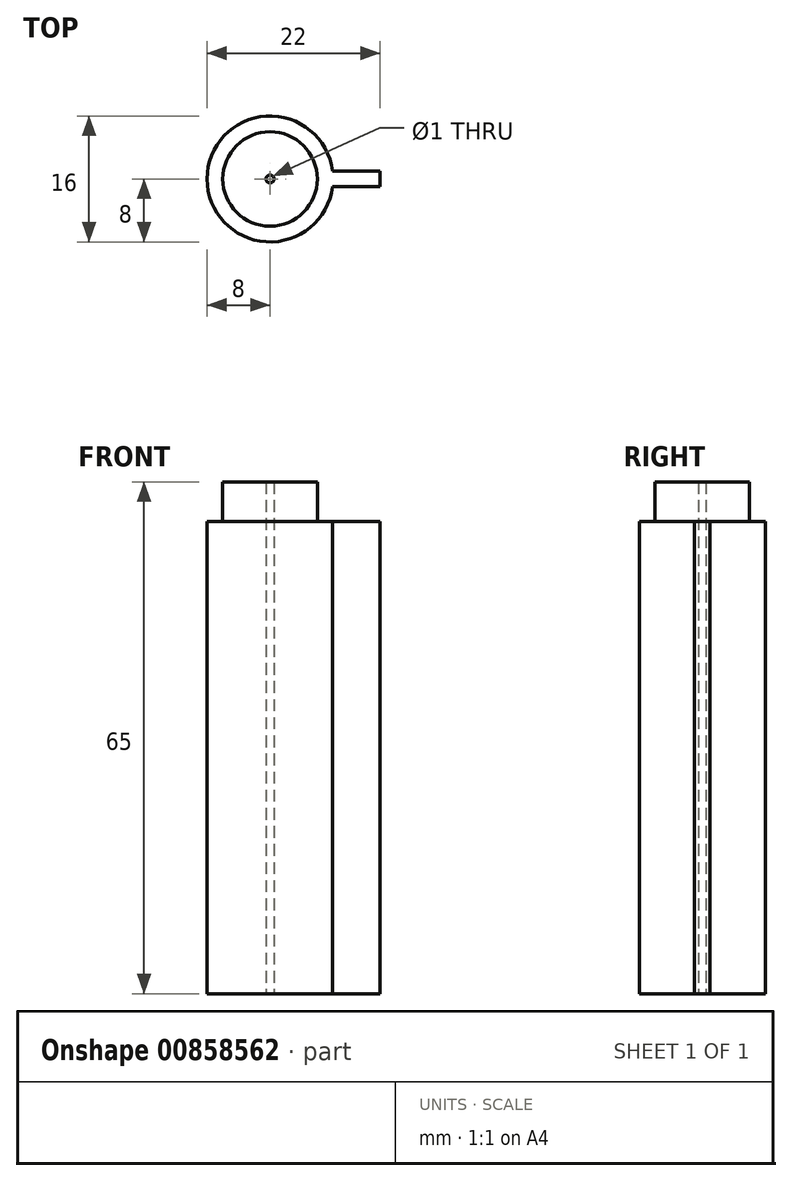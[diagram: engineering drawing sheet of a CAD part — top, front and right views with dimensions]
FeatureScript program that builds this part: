
annotation { "Feature Type Name" : "Feature", "Feature Type Description" : "" }
export const myFeature = defineFeature(function(context is Context, id is Id, definition is map)
    precondition{}
    {
        {
            var Q0;
            Q0=qCreatedBy(makeId("Top.planeOp"),FACE);
            var sketch = newSketch(context, id + "F0", { "sketchPlane" : qUnion([Q0])});
            skLineSegment(sketch, "E0.bottom", {"start": v(14, 14) * mm, "end": v(-14, 14) * mm});
            skLineSegment(sketch, "E0.top", {"start": v(14, -14) * mm, "end": v(-14, -14) * mm});
            skLineSegment(sketch, "E0.left", {"start": v(14, 14) * mm, "end": v(14, -14) * mm});
            skLineSegment(sketch, "E0.right", {"start": v(-14, 14) * mm, "end": v(-14, -14) * mm});
            skPoint(sketch, "E0.middle", {"position": v(0, 0) * mm});
            skCircle(sketch, "E1", {"center": v(0, 0) * mm, "radius": 6 * mm});
            skArc(sketch, "E2.0", {"start": v(7.94, 1) * mm, "mid": v(-8, 0) * mm, "end": v(7.94, -1) * mm});
            skLineSegment(sketch, "E3.bottom", {"start": v(7.94, 1) * mm, "end": v(14, 1) * mm});
            skLineSegment(sketch, "E3.top", {"start": v(7.94, -1) * mm, "end": v(14, -1) * mm});
            skLineSegment(sketch, "E3.left", {"start": v(0, 1) * mm, "end": v(0, -1) * mm});
            skLineSegment(sketch, "E3.right", {"start": v(14, 1) * mm, "end": v(14, -1) * mm});
            skLineSegment(sketch, "E4.1.0", {"start": v(-1, 14) * mm, "end": v(1, 14) * mm});
            skLineSegment(sketch, "E4.1.1", {"start": v(1, 7.94) * mm, "end": v(1, 14) * mm});
            skLineSegment(sketch, "E4.1.2", {"start": v(-1, 7.94) * mm, "end": v(-1, 14) * mm});
            skLineSegment(sketch, "E4.2.0", {"start": v(-14, -1) * mm, "end": v(-14, 1) * mm});
            skLineSegment(sketch, "E4.2.1", {"start": v(-7.94, 1) * mm, "end": v(-14, 1) * mm});
            skLineSegment(sketch, "E4.2.2", {"start": v(-7.94, -1) * mm, "end": v(-14, -1) * mm});
            skLineSegment(sketch, "E4.3.0", {"start": v(1, -14) * mm, "end": v(-1, -14) * mm});
            skLineSegment(sketch, "E4.3.1", {"start": v(-1, -7.94) * mm, "end": v(-1, -14) * mm});
            skLineSegment(sketch, "E4.3.2", {"start": v(1, -7.94) * mm, "end": v(1, -14) * mm});
            skLineSegment(sketch, "E5.0", {"start": v(16, 20.35) * mm, "end": v(-14, 20.35) * mm});
            skLineSegment(sketch, "E6.bottom", {"start": v(16.5, 16.5) * mm, "end": v(-16.5, 16.5) * mm});
            skLineSegment(sketch, "E6.top", {"start": v(16.5, -16.5) * mm, "end": v(-16.5, -16.5) * mm});
            skLineSegment(sketch, "E6.left", {"start": v(16.5, 16.5) * mm, "end": v(16.5, -16.5) * mm});
            skLineSegment(sketch, "E6.right", {"start": v(-16.5, 16.5) * mm, "end": v(-16.5, -16.5) * mm});
            skCircle(sketch, "E7", {"center": v(0, 0) * mm, "radius": 0.5 * mm});
            skSolve(sketch);
        }
        {
            var Q0;
            {var subQ1=sQuery(id+"F0.wireOp",EDGE,"E3.right");Q0=makeQuery(id+"F0.imprint","IMPRINT",FACE,{"disambiguationData":[TD([[makeQuery(id+"F0.imprint","IMPRINT",EDGE,{"derivedFrom":subQ1}),1.0]])]});}
            var Q1;
            Q1=makeQuery(id+"F0.imprint","IMPRINT",FACE,{"disambiguationData":[TD([[makeQuery(id+"F0.imprint","IMPRINT",EDGE,{"derivedFrom":sQuery(id+"F0.wireOp",EDGE,"E1")}),-1.0]])]});
            var Q2;
            Q2=makeQuery(id+"F0.imprint","IMPRINT",FACE,{"disambiguationData":[TD([[makeQuery(id+"F0.imprint","IMPRINT",EDGE,{"derivedFrom":sQuery(id+"F0.wireOp",EDGE,"E4.2.0")}),-1.0]])]});
            var Q3;
            Q3=makeQuery(id+"F0.imprint","IMPRINT",FACE,{"disambiguationData":[TD([[makeQuery(id+"F0.imprint","IMPRINT",EDGE,{"derivedFrom":sQuery(id+"F0.wireOp",EDGE,"E4.3.0")}),-1.0]])]});
            var Q4;
            Q4=makeQuery(id+"F0.imprint","IMPRINT",FACE,{"disambiguationData":[TD([[makeQuery(id+"F0.imprint","IMPRINT",EDGE,{"derivedFrom":sQuery(id+"F0.wireOp",EDGE,"E4.1.0")}),-1.0]])]});
            extrude(context, id + "F1", {"entities" : qUnion([Q0, Q1, Q2, Q3, Q4]), "depth" : 60 * mm, "offsetDistance" : 25.4 * mm});
        }
        {
            var Q0;
            Q0=makeQuery(id+"F0.imprint","IMPRINT",FACE,{"disambiguationData":[TD([[makeQuery(id+"F0.imprint","IMPRINT",EDGE,{"derivedFrom":sQuery(id+"F0.wireOp",EDGE,"E1")}),1.0]])]});
            extrude(context, id + "F2", {"entities" : qUnion([Q0]), "operationType" : NewBodyOperationType.ADD, "depth" : 65 * mm, "offsetDistance" : 25.4 * mm});
        }
    });
